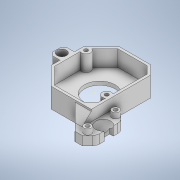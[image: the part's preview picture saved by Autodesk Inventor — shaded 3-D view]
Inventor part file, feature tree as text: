
AUTODESK INVENTOR PART (.ipt)
format: ipt  version: 2020 (Build 240168000, 168)  size: 607,744 bytes
history: native  units: mm
features: sketch x33, extrude x29, projected_geometry x13, chamfer x4, plane x1, revolve x1, fillet x1, hole x1
ambient origin geometry x8: Origin, YZ Plane, XZ Plane, XY Plane, X Axis, Y Axis, Z Axis, Center Point
bodies: Volumenkörper1 (feature_tree)
feature tree (83):
  extrude  "Extrusion1"  Depth=21.5mm
  extrude  "Extrusion2"  Depth=5.5mm
  extrude  "Extrusion3"  Depth=5.5mm
  extrude  "Extrusion7"  Depth=5.5mm
  extrude  "Extrusion8"  Depth=5.5mm
  extrude  "Extrusion15"  Depth=2.0mm
  extrude  "Extrusion16"  Depth=5.5mm
  plane  "Arbeitsebene1"
  revolve  "Umdrehung1"
  extrude  "Extrusion17"  Depth=5.5mm
  extrude  "Extrusion18"  Depth=5.5mm
  extrude  "Extrusion19"  Depth=5.5mm
  extrude  "Extrusion20"  Depth=2.0mm TaperAngle=0.0deg
  sketch  "Skizze24"  dims[d26=2.0mm]
  extrude  "Extrusion21"  Depth=2.0mm
  sketch  "Skizze26"  dims[d28=4.0mm]
  chamfer  "Fase2"  Distance=5.0mm
  fillet  "Rundung2"  Radius=5.0mm
  extrude  "Extrusion22"  Depth=8.0mm TaperAngle=0.0deg
  extrude  "Extrusion23"  Depth=0.5mm
  extrude  "Extrusion24"  Depth=5.0mm
  extrude  "Extrusion25"  Depth=5.0mm
  extrude  "Extrusion26"  Depth=5.0mm
  extrude  "Extrusion27"  Depth=5.0mm
  extrude  "Extrusion28"  Depth=10.0mm TaperAngle=0.0deg
  extrude  "Extrusion29"  Depth=8.5mm
  extrude  "Extrusion30"  Depth=7.0mm TaperAngle=0.0deg
  extrude  "Extrusion31"  Depth=4.0mm TaperAngle=0.0deg
  extrude  "Extrusion32"  Depth=4.0mm
  extrude  "Extrusion33"  Depth=4.0mm
  extrude  "Extrusion34"  Depth=3.0mm
  extrude  "Extrusion35"  TaperAngle=0.0deg  [1 undecoded]
  extrude  "Extrusion36"  Depth=4.0mm
  chamfer  "Fase3"  Distance=3.0mm
  chamfer  "Fase4"  Distance=4.0mm Angle=45.0deg
  chamfer  "Fase5"  Distance=4.0mm
  extrude  "Extrusion37"  Depth=10.0mm TaperAngle=0.0deg
  extrude  "Extrusion38"  Depth=8.0mm
  hole  "Bohrung1"  [1 undecoded]
  sketch  "Skizze1"  dims[d0=21.5mm d1=55.0mm]
  sketch  "Skizze3"  dims[d2=5.5mm d3=5.5mm]
  projected_geometry  "Projizierte Kontur1"
  sketch  "Skizze4"  dims[d4=5.5mm d5=5.5mm]
  sketch  "Skizze8"  dims[d6=5.5mm d7=5.5mm]
  sketch  "Skizze9"  dims[d8=5.5mm d9=5.5mm]
  sketch  "Skizze17"  dims[d10=2.0mm d11=2.0mm]
  sketch  "Skizze18"  dims[d12=5.5mm d13=5.5mm]
  projected_geometry  "Projizierte Kontur5"
  sketch  "Skizze19"  dims[d14=5.5mm d15=5.5mm]
  sketch  "Skizze20"  dims[d16=5.5mm d17=5.5mm]
  sketch  "Skizze21"  dims[d18=5.5mm d19=5.5mm]
  sketch  "Skizze22"  dims[d20=10.0mm d21=0.0mm d22=2.0mm d23=0.0mm]
  sketch  "Skizze23"  dims[d24=2.0mm d25=21.0mm]
  sketch  "Skizze25"  dims[d27=18.3mm]
  sketch  "Skizze27"  dims[d29=4.0mm]
  projected_geometry  "Projizierte Kontur6"
  projected_geometry  "Projizierte Kontur7"
  sketch  "Skizze28"  dims[d30=1.1mm]
  sketch  "Skizze29"  dims[d31=1.1mm d32=5.0mm d33=0.0mm d44=5.0mm]
  projected_geometry  "Projizierte Kontur8"
  sketch  "Skizze30"  dims[d45=8.0mm d46=0.0mm d47=12.0mm d48=0.0mm]
  sketch  "Skizze31"  dims[d74=0.5mm d75=0.5mm]
  projected_geometry  "Projizierte Kontur9"
  projected_geometry  "Projizierte Kontur10"
  sketch  "Skizze32"  dims[d80=5.0mm d81=5.0mm]
  sketch  "Skizze33"  dims[d82=5.0mm d83=5.0mm]
  sketch  "Skizze34"  dims[d84=5.0mm d85=5.0mm]
  projected_geometry  "Projizierte Kontur11"
  sketch  "Skizze35"  dims[d86=5.0mm d87=5.0mm]
  projected_geometry  "Projizierte Kontur12"
  sketch  "Skizze36"  dims[d88=10.0mm d89=0.0mm d90=10.0mm d91=0.0mm]
  projected_geometry  "Projizierte Kontur13"
  sketch  "Skizze37"  dims[d92=-6.0mm d93=8.5mm]
  sketch  "Skizze38"  dims[d94=90.0deg d95=7.0mm d96=0.0mm]
  sketch  "Skizze39"  dims[d97=5.0mm d98=4.0mm d99=0.0mm]
  projected_geometry  "Projizierte Kontur14"
  sketch  "Skizze40"  dims[d100=2.0mm d101=0.0mm d102=4.0mm]
  sketch  "Skizze41"  dims[d103=3.0mm d104=4.0mm]
  sketch  "Skizze42"  dims[d105=3.0mm d106=2.1mm]
  projected_geometry  "Projizierte Kontur15"
  sketch  "Skizze43"  dims[d107=2.1mm d108=0.0mm d109=0.0mm]
  projected_geometry  "Projizierte Kontur16"
  sketch  "Skizze44"  dims[d110=4.0mm d111=4.0mm d112=3.0mm d113=0.0mm d114=4.0mm d115=2.0mm d116=45.0deg d117=4.0mm d118=10.0mm d119=0.0mm d120=3.6mm d121=10.0mm d122=5.0mm d123=2.1mm d124=13.0mm d125=11.7mm d126=2.1mm d127=5.0mm d128=9.0mm d129=0.0mm d130=5.0mm d131=0.0mm d132=38.0mm d133=29.6mm d134=10.0mm d135=10.0mm d136=10.0mm d137=10.0mm d138=5.0mm d139=5.0mm d140=5.0mm d141=0.0mm d142=0.0mm d143=0.0mm d144=0.0mm d145=0.0mm d146=17.0mm d147=0.0mm d148=0.0mm d149=1.4mm d150=1.4mm d151=1.4mm d152=1.4mm d153=1.4mm d154=1.4mm d155=1.4mm d156=9.0mm d157=0.0mm d158=9.0mm d159=0.0mm d160=10.0mm d161=0.0mm d162=10.0mm d163=0.0mm d164=2.1mm d165=1.05mm d166=1.05mm d167=9.0mm d168=0.0mm d169=5.0mm d170=10.0mm d171=0.0mm d172=2.0mm d173=0.0mm d174=5.0mm d175=3.0mm d177=4.0mm d178=4.0mm d179=3.0mm d180=5.0mm d181=0.0mm d182=2.0mm d183=2.0mm d184=45.0deg d185=9.0mm d186=2.0mm d187=45.0deg d188=5.0mm d189=2.0mm d190=45.0deg d191=5.0mm d192=0.0mm d193=6.0mm d194=0.0mm d195=5.2mm d196=6.0mm d197=4.0mm d198=2.0mm d199=90.0deg d200=8.0mm d201=20.594885mm]
note: 2 required parameter values undecoded (feature->parameter linkage not recoverable at this tier; creation-order binding heuristic only, values carry confidence <= 0.55)
